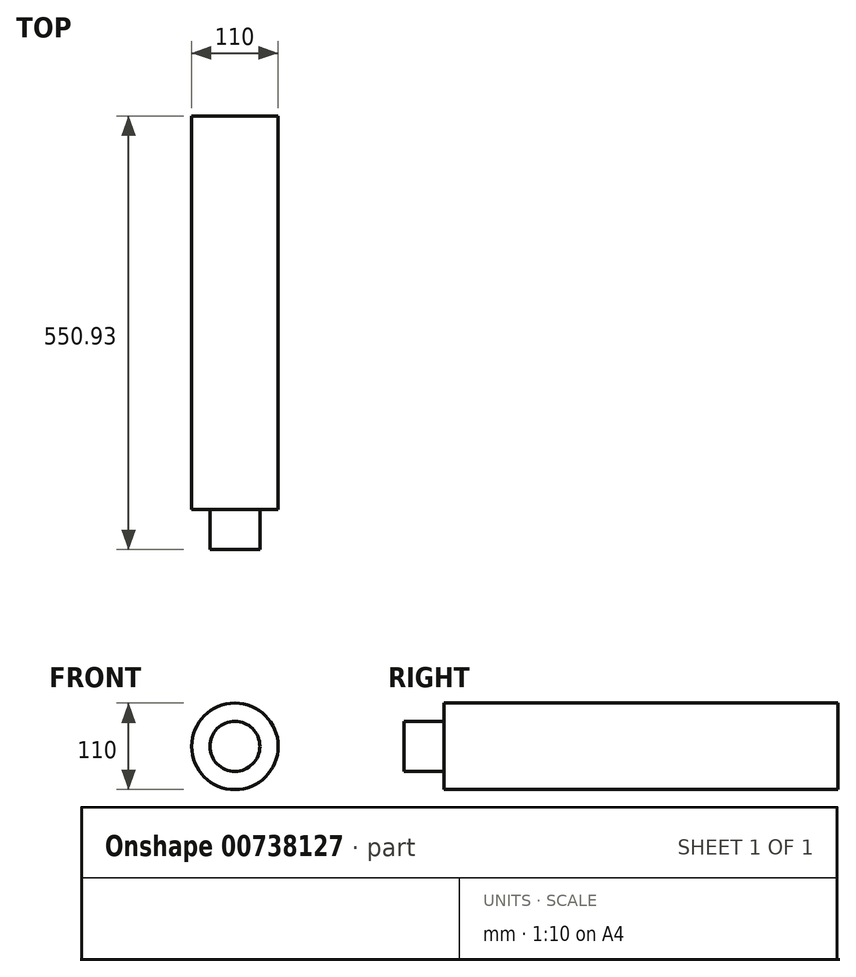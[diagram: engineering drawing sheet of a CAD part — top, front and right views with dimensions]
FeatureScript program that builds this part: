
annotation { "Feature Type Name" : "Feature", "Feature Type Description" : "" }
export const myFeature = defineFeature(function(context is Context, id is Id, definition is map)
    precondition{}
    {
        {
            var Q0;
            Q0=qCreatedBy(makeId("Front.planeOp"),FACE);
            var sketch = newSketch(context, id + "F0", { "sketchPlane" : qUnion([Q0])});
            skCircle(sketch, "E0", {"center": v(0, 0) * mm, "radius": 55 * mm});
            skSolve(sketch);
        }
        {
            var Q0;
            Q0 = qSketchRegion(id + "F0", true);
            extrude(context, id + "F1", {"entities" : qUnion([Q0]), "oppositeDirection" : true, "depth" : 500.13 * mm, "offsetDistance" : 25.4 * mm});
        }
        {
            var Q0;
            Q0=makeQuery(id+"F1.opExtrude","CAP_FACE",FACE,{"disambiguationData":[OSD([sQuery(id+"F0.wireOp",EDGE,"E0")])],"isStart":true});
            var sketch = newSketch(context, id + "F2", { "sketchPlane" : qUnion([Q0])});
            skCircle(sketch, "E1", {"center": v(0, 0) * mm, "radius": 31.75 * mm});
            skSolve(sketch);
        }
        {
            var Q0;
            Q0 = qSketchRegion(id + "F2", true);
            extrude(context, id + "F3", {"entities" : qUnion([Q0]), "operationType" : NewBodyOperationType.ADD, "depth" : 50.8 * mm, "offsetDistance" : 25.4 * mm});
        }
    });
